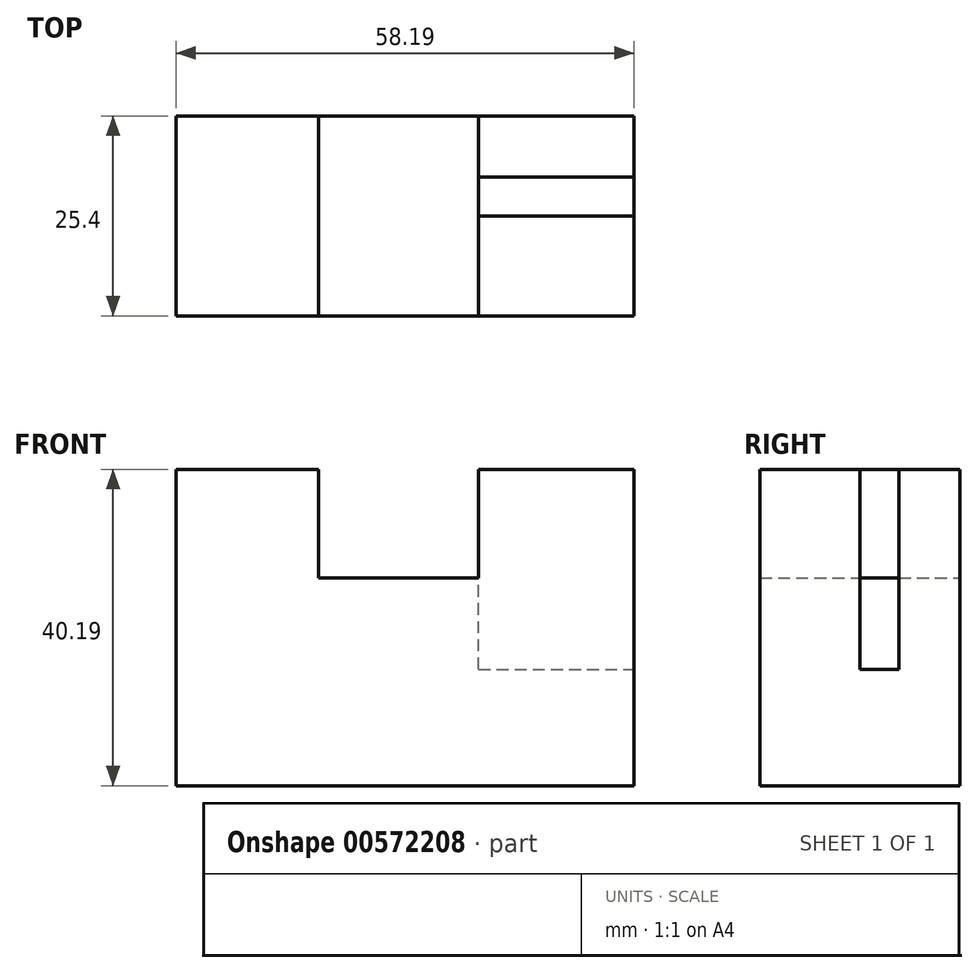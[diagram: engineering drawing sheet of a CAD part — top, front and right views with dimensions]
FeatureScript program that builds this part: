
annotation { "Feature Type Name" : "Feature", "Feature Type Description" : "" }
export const myFeature = defineFeature(function(context is Context, id is Id, definition is map)
    precondition{}
    {
        {
            var Q0;
            Q0=qCreatedBy(makeId("Front.planeOp"),FACE);
            var sketch = newSketch(context, id + "F0", { "sketchPlane" : qUnion([Q0])});
            skLineSegment(sketch, "E0.bottom", {"start": v(0, 0) * mm, "end": v(58.19, 0) * mm});
            skLineSegment(sketch, "E0.top", {"start": v(0, 40.19) * mm, "end": v(18.1, 40.19) * mm});
            skLineSegment(sketch, "E0.left", {"start": v(0, 0) * mm, "end": v(0, 40.19) * mm});
            skLineSegment(sketch, "E0.right", {"start": v(58.19, 0) * mm, "end": v(58.19, 40.19) * mm});
            skLineSegment(sketch, "E1.top", {"start": v(18.1, 26.39) * mm, "end": v(38.42, 26.39) * mm});
            skLineSegment(sketch, "E1.left", {"start": v(18.1, 40.19) * mm, "end": v(18.1, 26.39) * mm});
            skLineSegment(sketch, "E1.right", {"start": v(38.42, 40.19) * mm, "end": v(38.42, 26.39) * mm});
            skLineSegment(sketch, "E2.trimOffspring", {"start": v(38.42, 40.19) * mm, "end": v(58.19, 40.19) * mm});
            skSolve(sketch);
        }
        {
            var Q0;
            Q0 = qSketchRegion(id + "F0", true);
            extrude(context, id + "F1", {"entities" : qUnion([Q0]), "depth" : 25.4 * mm, "offsetDistance" : 25.4 * mm});
        }
        {
            var Q0;
            Q0=makeQuery(id+"F1.opExtrude","SWEPT_FACE",FACE,{"disambiguationData":[OSD([sQuery(id+"F0.wireOp",EDGE,"E2.trimOffspring")])]});
            var sketch = newSketch(context, id + "F2", { "sketchPlane" : qUnion([Q0])});
            skLineSegment(sketch, "E3.bottom", {"start": v(38.42, -12.7) * mm, "end": v(58.19, -12.7) * mm});
            skLineSegment(sketch, "E3.top", {"start": v(38.42, -7.77) * mm, "end": v(58.19, -7.77) * mm});
            skLineSegment(sketch, "E3.left", {"start": v(38.42, -12.7) * mm, "end": v(38.42, -7.77) * mm});
            skLineSegment(sketch, "E3.right", {"start": v(58.19, -12.7) * mm, "end": v(58.19, -7.77) * mm});
            skSolve(sketch);
        }
        {
            var Q0;
            Q0 = qSketchRegion(id + "F2", true);
            extrude(context, id + "F3", {"entities" : qUnion([Q0]), "operationType" : NewBodyOperationType.REMOVE, "oppositeDirection" : true, "depth" : 25.4 * mm, "offsetDistance" : 25.4 * mm});
        }
    });
